# Revit family: Accessory-Flush_Actuator_Plate-KOHLER-Conceal-K-31209T_1
name_source: partatom
category: Specialty Equipment
units: mm (PartAtom-declared; Revit-internal decimal feet)

## family parameters
Cut with Voids When Loaded = No
Host = Face
OmniClass Number = 23.31.25.00
OmniClass Title = Toilet and Bath Specialties
Part Type = Normal
Room Calculation Point = No
Round Connector Dimension = Use Diameter
Shared = No

## types (4) — shared parameters
ADA Compliant = No
Assembly Code = C1030200
Date Modified = 08/17/2022
Default Elevation = 42"
Description = Pneumatic In-Wall Tank Faceplate
Height = 6 5/16"
Length = 8 7/8"
Manufacturer = Kohler Co.
Master Format 2014 = 10 28 00
Master Format 2014 Name = Toilet, Bath, and Laundry Accessories
Material = Premium Metal Construction
Product Name = Conceal
URL = http://www.kohler.com.cn
WaterSense Certified = No
Width = 3/16"

## per-type parameters (varying)
| type | Finish | Model | Type |
| CP-Polished Chrome | Kohler-Metal-CP-Polished_Chrome | K-31209T-PNE-CP | 1 |
| With PVD, 2BL-Black | KOHLER-Metal-2BL-Black | K-31209T-PNEF-2BL | 2 |
| With PVD, BV-Brushed Bronze | Kohler-Metal-BV-Brushed_Bronze | K-31209T-PNEF-BV | 3 |
| With PVD, BN-Vibrant Brushed Nickel | Kohler-Metal-BN-Vibrant_Brushed_Nickel | K-31209T-PNEF-BN | 4 |

## geometry (parser evidence)
native form markers: Sweep x5
no freeform markers — native parametric forms only
